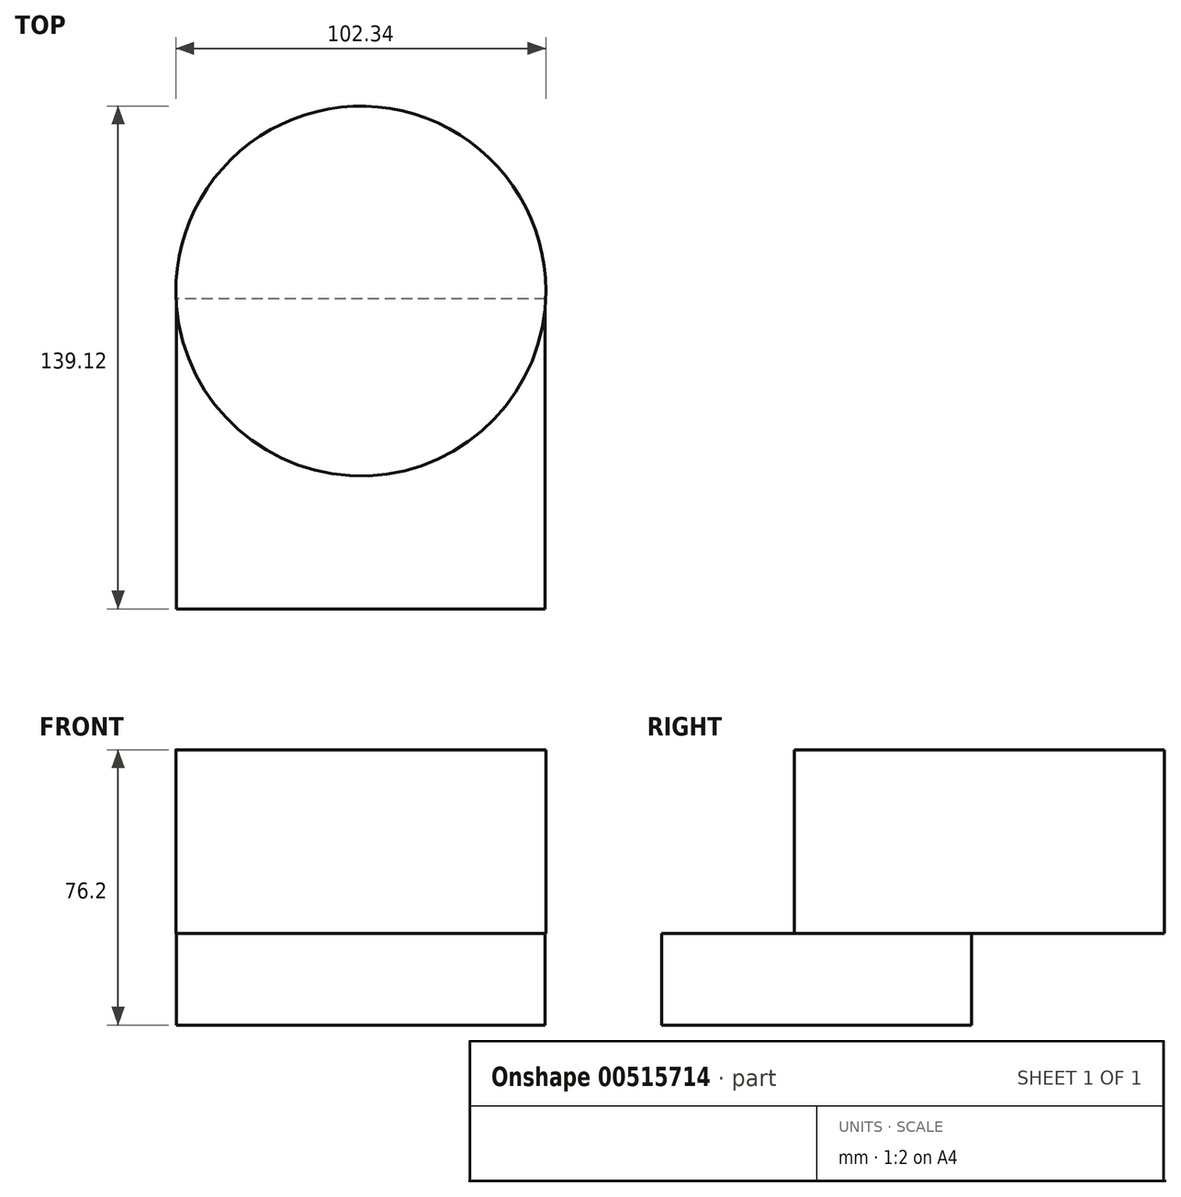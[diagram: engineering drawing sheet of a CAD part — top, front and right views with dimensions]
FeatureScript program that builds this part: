
annotation { "Feature Type Name" : "Feature", "Feature Type Description" : "" }
export const myFeature = defineFeature(function(context is Context, id is Id, definition is map)
    precondition{}
    {
        {
            var Q0;
            Q0=qCreatedBy(makeId("Top.planeOp"),FACE);
            var sketch = newSketch(context, id + "F0", { "sketchPlane" : qUnion([Q0])});
            skLineSegment(sketch, "E0.bottom", {"start": v(51, 42.87) * mm, "end": v(-51, 42.87) * mm});
            skLineSegment(sketch, "E0.top", {"start": v(51, -42.87) * mm, "end": v(-51, -42.87) * mm});
            skLineSegment(sketch, "E0.left", {"start": v(51, 42.87) * mm, "end": v(51, -42.87) * mm});
            skLineSegment(sketch, "E0.right", {"start": v(-51, 42.87) * mm, "end": v(-51, -42.87) * mm});
            skPoint(sketch, "E0.middle", {"position": v(0, 0) * mm});
            skSolve(sketch);
        }
        {
            var Q0;
            Q0 = qSketchRegion(id + "F0", true);
            var sketch = newSketch(context, id + "F1", { "sketchPlane" : qUnion([Q0])});
            skCircle(sketch, "E1", {"center": v(0, 45.09) * mm, "radius": 51.17 * mm});
            skSolve(sketch);
        }
        {
            var Q0;
            Q0 = qSketchRegion(id + "F1", true);
            extrude(context, id + "F2", {"entities" : qUnion([Q0]), "depth" : 50.8 * mm, "offsetDistance" : 25.4 * mm});
        }
        {
            var Q0;
            Q0=makeQuery(id+"F0.imprint","IMPRINT",FACE,{"disambiguationData":[TD([[makeQuery(id+"F0.imprint","IMPRINT",EDGE,{"derivedFrom":sQuery(id+"F0.wireOp",EDGE,"E0.bottom")}),1.0]])]});
            extrude(context, id + "F3", {"entities" : qUnion([Q0]), "operationType" : NewBodyOperationType.ADD, "oppositeDirection" : true, "depth" : 25.4 * mm, "offsetDistance" : 25.4 * mm});
        }
    });
